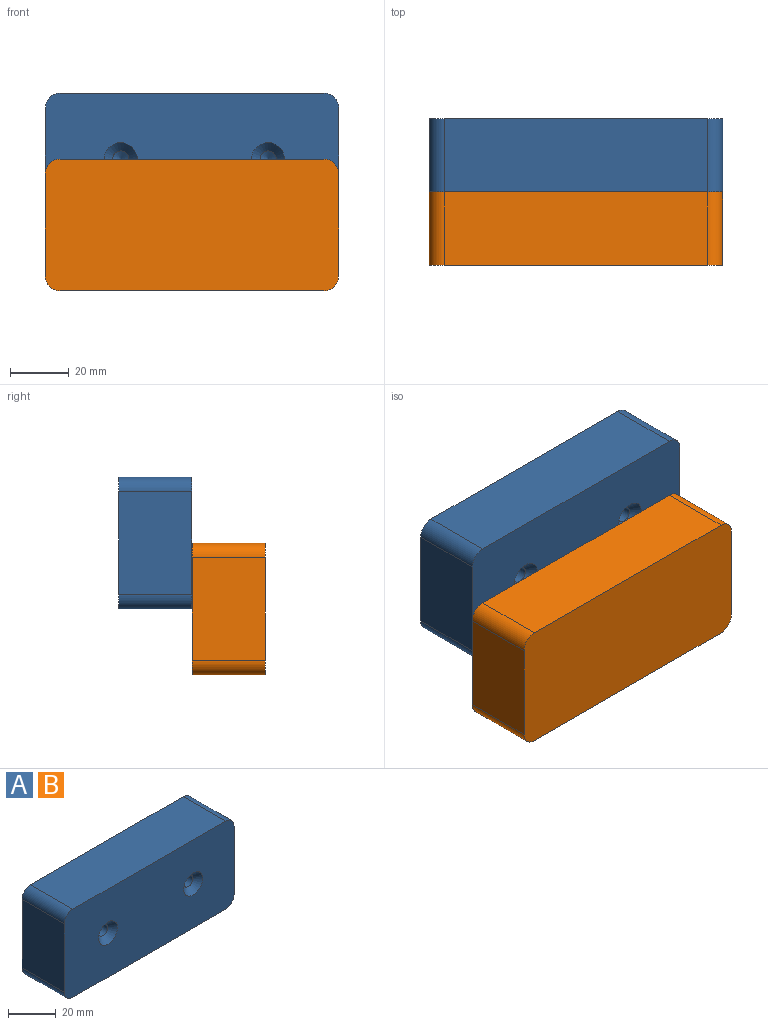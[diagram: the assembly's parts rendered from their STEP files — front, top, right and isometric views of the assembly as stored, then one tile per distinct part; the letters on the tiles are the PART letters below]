
ASSEMBLY  parts=2 mates=1
PART A: 32 faces, bbox 100x25x45 mm
  f0: plane 35x25mm, normal (-1,0,0), area 875mm2, adj f4,f5,f12,f15
  f1: plane 90x25mm, normal (0,0,-1), area 2250mm2, adj f4,f5,f12,f13
  f2: plane 35x25mm, normal (1,0,0), area 875mm2, adj f4,f5,f13,f14
  f3: plane 90x25mm, normal (0,0,1), area 2250mm2, adj f4,f5,f14,f15
  f4: plane 100x45mm, normal (0,-1,0), area 4281.5mm2, adj f0,f1,f2,f3,f8,f11,f12,f13
  f5: plane 100x45mm, normal (0,1,0), area 4478.5mm2, adj f0,f1,f2,f3,f12,f13,f14,f15
  f6: cone r=0mm half-angle=59deg, axis (0,-1,0), area 27.7mm2, adj f7
  f7: cylinder r=2.75mm len=11.55mm, axis (0,-1,0), area 199.6mm2, adj f6,f8
  f8: cone r=2.75mm half-angle=45deg, axis (0,-1,0), area 105.7mm2, adj f4,f7
  f9: cone r=0mm half-angle=59deg, axis (0,-1,0), area 27.7mm2, adj f10
  f10: cylinder r=2.75mm len=11.55mm, axis (0,-1,0), area 199.6mm2, adj f9,f11
  f11: cone r=2.75mm half-angle=45deg, axis (0,-1,0), area 105.7mm2, adj f4,f10
  f12: cylinder r=5mm len=25mm, axis (0,-1,0), area 196.3mm2, adj f0,f1,f4,f5
  f13: cylinder r=5mm len=25mm, axis (0,1,0), area 196.3mm2, adj f1,f2,f4,f5
  f14: cylinder r=5mm len=25mm, axis (0,-1,0), area 196.3mm2, adj f2,f3,f4,f5
  f15: cylinder r=5mm len=25mm, axis (0,1,0), area 196.3mm2, adj f0,f3,f4,f5
  f16: plane 35x20mm, normal (1,0,0), area 700mm2, adj f20,f21,f28,f31
  f17: plane 90x20mm, normal (0,0,1), area 1800mm2, adj f20,f21,f28,f29
  f18: plane 35x20mm, normal (-1,0,0), area 700mm2, adj f20,f21,f29,f30
  f19: plane 90x20mm, normal (0,0,-1), area 1800mm2, adj f20,f21,f30,f31
  f20: plane 95x40mm, normal (0,1,0), area 3518mm2, adj f16,f17,f18,f19,f24,f27,f28,f29
  f21: plane 95x40mm, normal (0,-1,0), area 3794.6mm2, adj f16,f17,f18,f19,f28,f29,f30,f31
  f22: cone r=1.29mm half-angle=59deg, axis (0,-1,0), area 101mm2, adj f23
  f23: cylinder r=5.25mm len=11.93mm, axis (0,-1,0), area 393.5mm2, adj f22,f24
  f24: cone r=4.52mm half-angle=45deg, axis (0,-1,0), area 73.2mm2, adj f20,f23
  f25: cone r=1.29mm half-angle=59deg, axis (0,-1,0), area 101mm2, adj f26
  f26: cylinder r=5.25mm len=11.93mm, axis (0,-1,0), area 393.5mm2, adj f25,f27
  f27: cone r=4.52mm half-angle=45deg, axis (0,-1,0), area 73.2mm2, adj f20,f26
  f28: cylinder r=2.5mm len=20mm, axis (0,-1,0), area 78.5mm2, adj f16,f17,f20,f21
  f29: cylinder r=2.5mm len=20mm, axis (0,1,0), area 78.5mm2, adj f17,f18,f20,f21
  f30: cylinder r=2.5mm len=20mm, axis (0,-1,0), area 78.5mm2, adj f18,f19,f20,f21
  f31: cylinder r=2.5mm len=20mm, axis (0,1,0), area 78.5mm2, adj f16,f19,f20,f21
PART B: same geometry as A
PLACE A t=(-25.23,-25.89,-9.93)mm
PLACE B rot(axis=(0,0,1),180deg) t=(-25.27,-75.89,-32.43)mm
MATE parallel B.f4 <-> A.f4  axis (0,1,0) through (-25.27,-50.89,-9.93)mm
